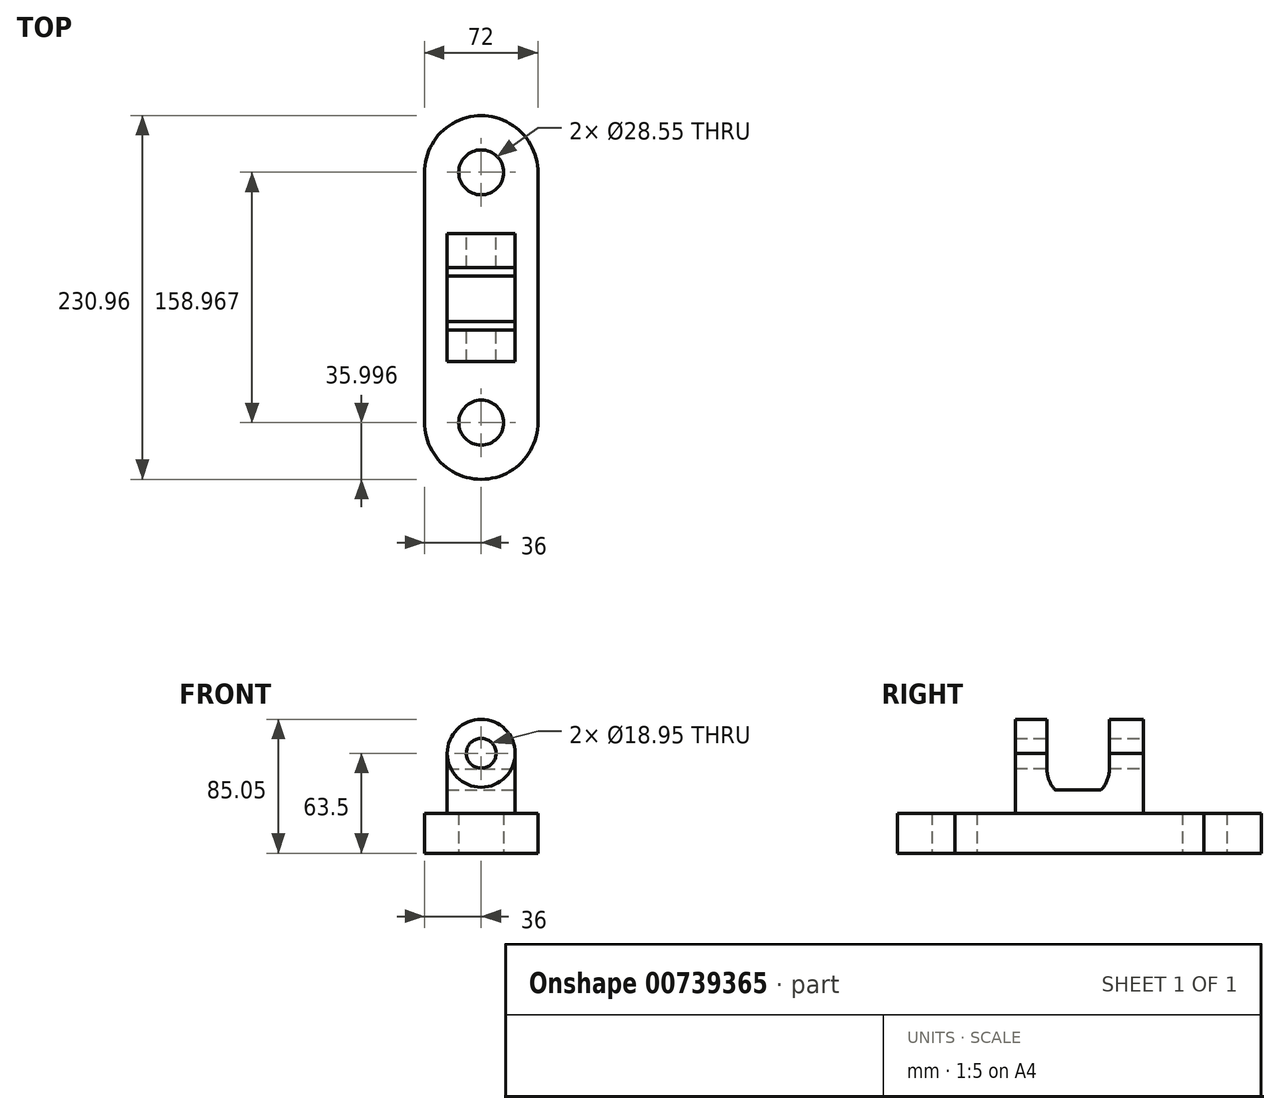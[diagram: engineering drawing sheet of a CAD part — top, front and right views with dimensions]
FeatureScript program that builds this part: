
annotation { "Feature Type Name" : "Feature", "Feature Type Description" : "" }
export const myFeature = defineFeature(function(context is Context, id is Id, definition is map)
    precondition{}
    {
        {
            var Q0;
            Q0=qCreatedBy(makeId("Top.planeOp"),FACE);
            var sketch = newSketch(context, id + "F0", { "sketchPlane" : qUnion([Q0])});
            skLineSegment(sketch, "E0.bottom", {"start": v(36, 79.48) * mm, "end": v(-36, 79.48) * mm});
            skLineSegment(sketch, "E0.top", {"start": v(36, -79.48) * mm, "end": v(-36, -79.48) * mm});
            skLineSegment(sketch, "E0.left", {"start": v(36, 79.48) * mm, "end": v(36, -79.48) * mm});
            skLineSegment(sketch, "E0.right", {"start": v(-36, 79.48) * mm, "end": v(-36, -79.48) * mm});
            skPoint(sketch, "E0.middle", {"position": v(0, 0) * mm});
            skSolve(sketch);
        }
        {
            var Q0;
            Q0=makeQuery(id+"F0.imprint","IMPRINT",FACE,{"disambiguationData":[TD([[makeQuery(id+"F0.imprint","IMPRINT",EDGE,{"derivedFrom":sQuery(id+"F0.wireOp",EDGE,"E0.bottom")}),1.0]])]});
            var sketch = newSketch(context, id + "F1", { "sketchPlane" : qUnion([Q0])});
            skCircle(sketch, "E1", {"center": v(0, 79.48) * mm, "radius": 36 * mm});
            skCircle(sketch, "E2", {"center": v(0, -79.48) * mm, "radius": 36 * mm});
            skSolve(sketch);
        }
        {
            var Q0;
            Q0=makeQuery(id+"F0.imprint","IMPRINT",FACE,{"disambiguationData":[TD([[makeQuery(id+"F0.imprint","IMPRINT",EDGE,{"derivedFrom":sQuery(id+"F0.wireOp",EDGE,"E0.bottom")}),1.0]])]});
            var sketch = newSketch(context, id + "F2", { "sketchPlane" : qUnion([Q0])});
            skCircle(sketch, "E3", {"center": v(0, 79.48) * mm, "radius": 14.28 * mm});
            skCircle(sketch, "E4", {"center": v(0, -79.48) * mm, "radius": 14.28 * mm});
            skSolve(sketch);
        }
        {
            var Q0;
            Q0=makeQuery(id+"F0.imprint","IMPRINT",FACE,{"disambiguationData":[TD([[makeQuery(id+"F0.imprint","IMPRINT",EDGE,{"derivedFrom":sQuery(id+"F0.wireOp",EDGE,"E0.bottom")}),1.0]])]});
            var sketch = newSketch(context, id + "F3", { "sketchPlane" : qUnion([Q0])});
            skLineSegment(sketch, "E5.bottom", {"start": v(21.63, 40.61) * mm, "end": v(-21.63, 40.61) * mm});
            skLineSegment(sketch, "E5.top", {"start": v(21.63, -40.61) * mm, "end": v(-21.63, -40.61) * mm});
            skLineSegment(sketch, "E5.left", {"start": v(21.63, 40.61) * mm, "end": v(21.63, -40.61) * mm});
            skLineSegment(sketch, "E5.right", {"start": v(-21.63, 40.61) * mm, "end": v(-21.63, -40.61) * mm});
            skPoint(sketch, "E5.middle", {"position": v(0, 0) * mm});
            skSolve(sketch);
        }
        {
            var Q0;
            Q0=makeQuery(id+"F0.imprint","IMPRINT",FACE,{"disambiguationData":[TD([[makeQuery(id+"F0.imprint","IMPRINT",EDGE,{"derivedFrom":sQuery(id+"F0.wireOp",EDGE,"E0.bottom")}),1.0]])]});
            var sketch = newSketch(context, id + "F4", { "sketchPlane" : qUnion([Q0])});
            skSolve(sketch);
        }
        {
            var Q0;
            Q0=makeQuery(id+"F4.imprint","IMPRINT",FACE,{"disambiguationData":[TD([[makeQuery(id+"F4.imprint","IMPRINT",EDGE,{"derivedFrom":makeQuery(id+"F0.imprint","IMPRINT",EDGE,{"derivedFrom":sQuery(id+"F0.wireOp",EDGE,"E0.bottom")})}),1.0]])]});
            extrude(context, id + "F5", {"entities" : qUnion([Q0]), "depth" : 25.4 * mm, "offsetDistance" : 25.4 * mm});
        }
        {
            var Q0;
            {var subQ5=makeQuery(id+"F0.imprint","IMPRINT",EDGE,{"derivedFrom":sQuery(id+"F0.wireOp",EDGE,"E0.bottom")});Q0=makeQuery(id+"F1.imprint","IMPRINT",FACE,{"disambiguationData":[TD([[makeQuery(id+"F1.imprint","IMPRINT",EDGE,{"derivedFrom":subQ5}),-1.0]])]});}
            var Q1;
            {var subQ5=makeQuery(id+"F0.imprint","IMPRINT",EDGE,{"derivedFrom":sQuery(id+"F0.wireOp",EDGE,"E0.top")});Q1=makeQuery(id+"F1.imprint","IMPRINT",FACE,{"disambiguationData":[TD([[makeQuery(id+"F1.imprint","IMPRINT",EDGE,{"derivedFrom":subQ5}),1.0]])]});}
            extrude(context, id + "F6", {"entities" : qUnion([Q0, Q1]), "operationType" : NewBodyOperationType.ADD, "depth" : 25.4 * mm, "offsetDistance" : 25.4 * mm});
        }
        {
            var Q0;
            Q0=makeQuery(id+"F3.imprint","IMPRINT",FACE,{"disambiguationData":[TD([[makeQuery(id+"F3.imprint","IMPRINT",EDGE,{"derivedFrom":sQuery(id+"F3.wireOp",EDGE,"E5.bottom")}),1.0]])]});
            extrude(context, id + "F7", {"entities" : qUnion([Q0]), "operationType" : NewBodyOperationType.ADD, "depth" : 63.5 * mm, "offsetDistance" : 25.4 * mm});
        }
        {
            var Q0;
            {var subQ0=sQuery(id+"F2.wireOp",EDGE,"E3");var subQ1=makeQuery(id+"F0.imprint","IMPRINT",EDGE,{"derivedFrom":sQuery(id+"F0.wireOp",EDGE,"E0.bottom")});var subQ2=makeQuery(id+"F2.imprint","INTERSECT",VERTEX,{"disambiguationData":[OD(0.0)],"derivedFrom":[subQ1,subQ0]});Q0=makeQuery(id+"F2.imprint","IMPRINT",FACE,{"disambiguationData":[TD([[makeQuery(id+"F2.imprint","IMPRINT",EDGE,{"disambiguationData":[TD([[subQ2,-1.0]])],"derivedFrom":subQ0}),1.0]])]});}
            var Q1;
            {var subQ0=sQuery(id+"F2.wireOp",EDGE,"E3");var subQ1=makeQuery(id+"F0.imprint","IMPRINT",EDGE,{"derivedFrom":sQuery(id+"F0.wireOp",EDGE,"E0.bottom")});var subQ2=makeQuery(id+"F2.imprint","INTERSECT",VERTEX,{"disambiguationData":[OD(0.0)],"derivedFrom":[subQ1,subQ0]});Q1=makeQuery(id+"F2.imprint","IMPRINT",FACE,{"disambiguationData":[TD([[makeQuery(id+"F2.imprint","IMPRINT",EDGE,{"disambiguationData":[TD([[subQ2,1.0]])],"derivedFrom":subQ0}),1.0]])]});}
            var Q2;
            Q2=sQuery(id+"F2.wireOp",EDGE,"E3");
            extrude(context, id + "F8", {"entities" : qUnion([Q0, Q1]), "operationType" : NewBodyOperationType.REMOVE, "surfaceEntities" : qUnion([Q2]), "depth" : 25.4 * mm, "offsetDistance" : 25.4 * mm});
        }
        {
            var Q0;
            {var subQ0=sQuery(id+"F2.wireOp",EDGE,"E4");var subQ1=makeQuery(id+"F0.imprint","IMPRINT",EDGE,{"derivedFrom":sQuery(id+"F0.wireOp",EDGE,"E0.top")});var subQ2=makeQuery(id+"F2.imprint","INTERSECT",VERTEX,{"disambiguationData":[OD(0.0)],"derivedFrom":[subQ1,subQ0]});Q0=makeQuery(id+"F2.imprint","IMPRINT",FACE,{"disambiguationData":[TD([[makeQuery(id+"F2.imprint","IMPRINT",EDGE,{"disambiguationData":[TD([[subQ2,1.0]])],"derivedFrom":subQ0}),1.0]])]});}
            var Q1;
            {var subQ0=sQuery(id+"F2.wireOp",EDGE,"E4");var subQ1=makeQuery(id+"F0.imprint","IMPRINT",EDGE,{"derivedFrom":sQuery(id+"F0.wireOp",EDGE,"E0.top")});var subQ2=makeQuery(id+"F2.imprint","INTERSECT",VERTEX,{"disambiguationData":[OD(0.0)],"derivedFrom":[subQ1,subQ0]});Q1=makeQuery(id+"F2.imprint","IMPRINT",FACE,{"disambiguationData":[TD([[makeQuery(id+"F2.imprint","IMPRINT",EDGE,{"disambiguationData":[TD([[subQ2,-1.0]])],"derivedFrom":subQ0}),1.0]])]});}
            extrude(context, id + "F9", {"entities" : qUnion([Q0, Q1]), "operationType" : NewBodyOperationType.REMOVE, "depth" : 25.4 * mm, "offsetDistance" : 25.4 * mm});
        }
        {
            var Q0;
            Q0=qCreatedBy(makeId("Front.planeOp"),FACE);
            var sketch = newSketch(context, id + "F10", { "sketchPlane" : qUnion([Q0])});
            skCircle(sketch, "E6", {"center": v(0, 63.5) * mm, "radius": 21.55 * mm});
            skCircle(sketch, "E7", {"center": v(0, 63.5) * mm, "radius": 9.48 * mm});
            skSolve(sketch);
        }
        {
            var Q0;
            Q0=makeQuery(id+"F10.imprint","IMPRINT",FACE,{"disambiguationData":[TD([[makeQuery(id+"F10.imprint","IMPRINT",EDGE,{"derivedFrom":sQuery(id+"F10.wireOp",EDGE,"E6")}),1.0]])]});
            extrude(context, id + "F11", {"entities" : qUnion([Q0]), "operationType" : NewBodyOperationType.ADD, "depth" : 40.64 * mm, "offsetDistance" : 25.4 * mm, "hasSecondDirection" : true, "secondDirectionOppositeDirection" : true, "secondDirectionDepth" : 40.64 * mm});
        }
        {
            var Q0;
            {var subQ0=sQuery(id+"F3.wireOp",EDGE,"E5.top");Q0=makeQuery(id+"F11.boolean.opBoolean","SPLIT",FACE,{"disambiguationData":[TD([makeQuery(id+"F11.opExtrude","SWEPT_FACE",FACE,{"disambiguationData":[OSD([sQuery(id+"F10.wireOp",EDGE,"E7")])]})])],"derivedFrom":makeQuery(id+"F7.opExtrude","SWEPT_FACE",FACE,{"disambiguationData":[OSD([subQ0])]})});}
            extrude(context, id + "F12", {"entities" : qUnion([Q0]), "operationType" : NewBodyOperationType.REMOVE, "oppositeDirection" : true, "depth" : 50.8 * mm, "offsetDistance" : 25.4 * mm, "hasSecondDirection" : true, "secondDirectionOppositeDirection" : false, "secondDirectionDepth" : 50.8 * mm});
        }
        {
            var Q0;
            {var subQ0=sQuery(id+"F3.wireOp",EDGE,"E5.bottom");Q0=makeQuery(id+"F11.boolean.opBoolean","SPLIT",FACE,{"disambiguationData":[TD([makeQuery(id+"F11.opExtrude","SWEPT_FACE",FACE,{"disambiguationData":[OSD([sQuery(id+"F10.wireOp",EDGE,"E7")])]})])],"derivedFrom":makeQuery(id+"F7.opExtrude","SWEPT_FACE",FACE,{"disambiguationData":[OSD([subQ0])]})});}
            extrude(context, id + "F13", {"entities" : qUnion([Q0]), "operationType" : NewBodyOperationType.REMOVE, "oppositeDirection" : true, "depth" : 101.6 * mm, "offsetDistance" : 25.4 * mm});
        }
        {
            var Q0;
            Q0=makeQuery(id+"F7.opExtrude","SWEPT_FACE",FACE,{"disambiguationData":[OSD([sQuery(id+"F3.wireOp",EDGE,"E5.left")])]});
            var sketch = newSketch(context, id + "F14", { "sketchPlane" : qUnion([Q0])});
            skLineSegment(sketch, "E8", {"start": v(19.05, 63.5) * mm, "end": v(19.05, 85.02) * mm});
            skLineSegment(sketch, "E9", {"start": v(19.05, 85.02) * mm, "end": v(-20.45, 85.02) * mm});
            skLineSegment(sketch, "E10", {"start": v(-20.45, 85.02) * mm, "end": v(-20.45, 63.5) * mm});
            skSolve(sketch);
        }
        {
            var Q0;
            Q0=makeQuery(id+"F14.imprint","IMPRINT",FACE,{"disambiguationData":[TD([[makeQuery(id+"F14.imprint","IMPRINT",EDGE,{"derivedFrom":sQuery(id+"F14.wireOp",EDGE,"E8")}),1.0]])]});
            var sketch = newSketch(context, id + "F15", { "sketchPlane" : qUnion([Q0])});
            skLineSegment(sketch, "E11.bottom", {"start": v(-20.7, 98.62) * mm, "end": v(18.95, 98.62) * mm});
            skLineSegment(sketch, "E11.top", {"start": v(-20.7, 40.11) * mm, "end": v(18.95, 40.11) * mm});
            skLineSegment(sketch, "E11.left", {"start": v(-20.7, 98.62) * mm, "end": v(-20.7, 40.11) * mm});
            skLineSegment(sketch, "E11.right", {"start": v(18.95, 98.62) * mm, "end": v(18.95, 40.11) * mm});
            skSolve(sketch);
        }
        {
            var Q0;
            {var subQ1=sQuery(id+"F15.wireOp",EDGE,"E11.bottom");Q0=makeQuery(id+"F15.imprint","IMPRINT",FACE,{"disambiguationData":[TD([[makeQuery(id+"F15.imprint","IMPRINT",EDGE,{"derivedFrom":subQ1}),-1.0]])]});}
            var sketch = newSketch(context, id + "F16", { "sketchPlane" : qUnion([Q0])});
            skLineSegment(sketch, "E12.bottom", {"start": v(-20.65, 98.62) * mm, "end": v(18.97, 98.62) * mm});
            skLineSegment(sketch, "E12.top", {"start": v(-20.65, 53.43) * mm, "end": v(18.97, 53.43) * mm});
            skLineSegment(sketch, "E12.left", {"start": v(-20.65, 98.62) * mm, "end": v(-20.65, 53.43) * mm});
            skLineSegment(sketch, "E12.right", {"start": v(18.97, 98.62) * mm, "end": v(18.97, 53.43) * mm});
            skSolve(sketch);
        }
        {
            var Q0;
            Q0 = qSketchRegion(id + "F16", true);
            extrude(context, id + "F17", {"entities" : qUnion([Q0]), "operationType" : NewBodyOperationType.REMOVE, "oppositeDirection" : true, "depth" : 76.2 * mm, "offsetDistance" : 25.4 * mm});
        }
        {
            var Q0;
            {var subQ2=sQuery(id+"F16.wireOp",EDGE,"E12.left");Q0=makeQuery(id+"F16.imprint","IMPRINT",FACE,{"disambiguationData":[TD([[makeQuery(id+"F16.imprint","IMPRINT",EDGE,{"derivedFrom":subQ2}),-1.0]])]});}
            var sketch = newSketch(context, id + "F18", { "sketchPlane" : qUnion([Q0])});
            skArc(sketch, "E13", {"start": v(-20.65, 54.07) * mm, "mid": v(-0.84, 33.78) * mm, "end": v(18.95, 54.1) * mm});
            skLineSegment(sketch, "E14", {"start": v(18.95, 54.1) * mm, "end": v(-20.65, 54.07) * mm});
            skSolve(sketch);
        }
        {
            var Q0;
            {var subQ0=sQuery(id+"F16.wireOp",EDGE,"E12.left");var subQ1=makeQuery(id+"F16.imprint","IMPRINT",EDGE,{"derivedFrom":subQ0});var subQ9=sQuery(id+"F18.wireOp",EDGE,"E13");var subQ10=makeQuery(id+"F18.imprint","INTERSECT",VERTEX,{"derivedFrom":[subQ1,subQ9]});Q0=makeQuery(id+"F18.imprint","IMPRINT",FACE,{"disambiguationData":[TD([[makeQuery(id+"F18.imprint","IMPRINT",EDGE,{"disambiguationData":[TD([[subQ10,-1.0]])],"derivedFrom":subQ9}),1.0]])]});}
            var Q1;
            {var subQ0=sQuery(id+"F18.wireOp",EDGE,"E13");var subQ1=makeQuery(id+"F16.imprint","IMPRINT",EDGE,{"derivedFrom":makeQuery(id+"F15.imprint","IMPRINT",EDGE,{"derivedFrom":sQuery(id+"F15.wireOp",EDGE,"E11.top")})});var subQ2=makeQuery(id+"F18.imprint","INTERSECT",VERTEX,{"disambiguationData":[OD(0.0)],"derivedFrom":[subQ1,subQ0]});Q1=makeQuery(id+"F18.imprint","IMPRINT",FACE,{"disambiguationData":[TD([[makeQuery(id+"F18.imprint","IMPRINT",EDGE,{"disambiguationData":[TD([[subQ2,-1.0]])],"derivedFrom":subQ0}),1.0]])]});}
            var Q2;
            {var subQ8=sQuery(id+"F18.wireOp",EDGE,"E14");Q2=makeQuery(id+"F18.imprint","IMPRINT",FACE,{"disambiguationData":[TD([[makeQuery(id+"F18.imprint","IMPRINT",EDGE,{"derivedFrom":subQ8}),1.0]])]});}
            extrude(context, id + "F19", {"entities" : qUnion([Q0, Q1, Q2]), "operationType" : NewBodyOperationType.REMOVE, "oppositeDirection" : true, "depth" : 76.2 * mm, "offsetDistance" : 25.4 * mm});
        }
    });
